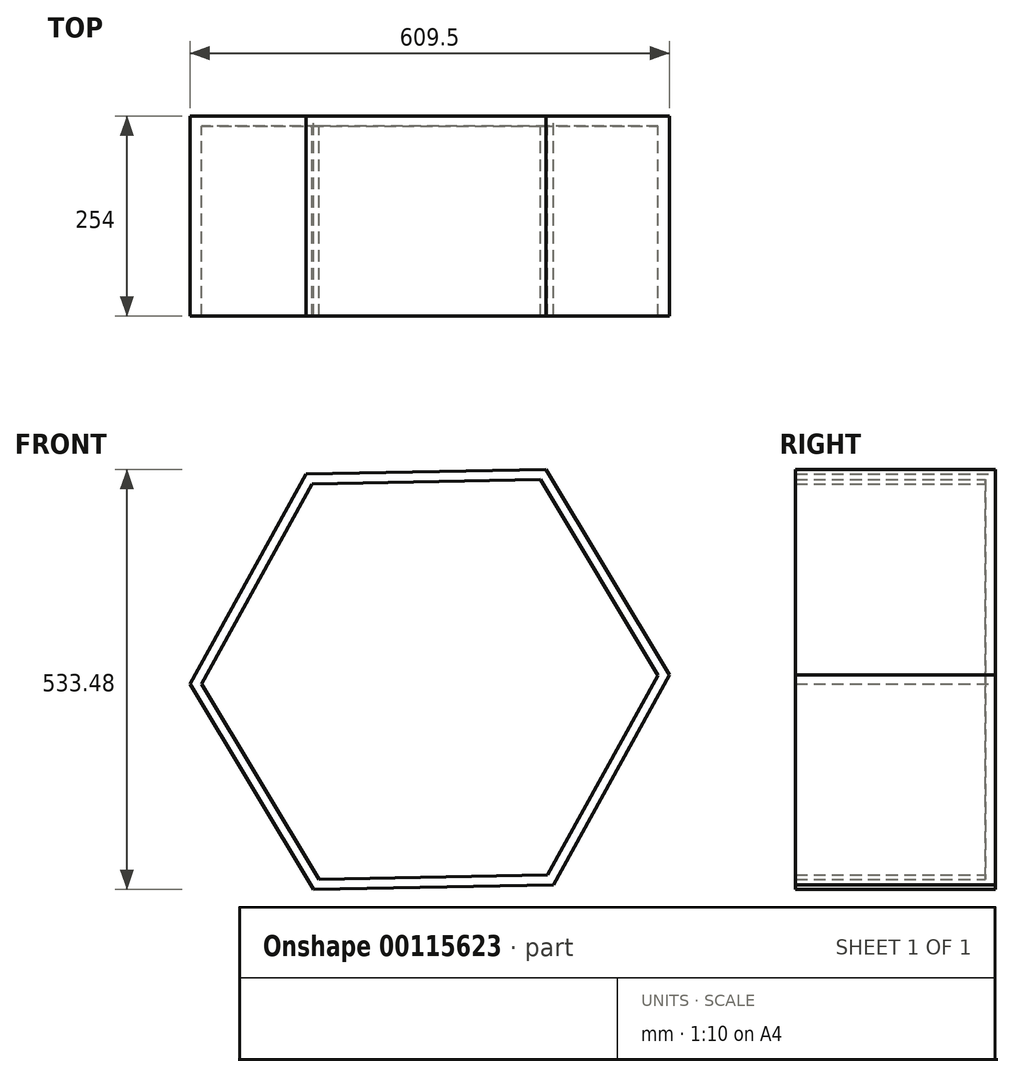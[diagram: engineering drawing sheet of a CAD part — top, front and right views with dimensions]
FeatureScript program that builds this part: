
annotation { "Feature Type Name" : "Feature", "Feature Type Description" : "" }
export const myFeature = defineFeature(function(context is Context, id is Id, definition is map)
    precondition{}
    {
        {
            var Q0;
            Q0=qCreatedBy(makeId("Front.planeOp"),FACE);
            var sketch = newSketch(context, id + "F0", { "sketchPlane" : qUnion([Q0])});
            skCircle(sketch, "E0.cCircle", {"center": v(0, 0) * mm, "radius": 263.96 * mm, "construction": true});
            skLineSegment(sketch, "E0.0", {"start": v(-304.75, -5.64) * mm, "end": v(-157.26, 261.1) * mm});
            skLineSegment(sketch, "E0.1", {"start": v(-157.26, 261.1) * mm, "end": v(147.5, 266.74) * mm});
            skLineSegment(sketch, "E0.2", {"start": v(147.5, 266.74) * mm, "end": v(304.75, 5.64) * mm});
            skLineSegment(sketch, "E0.3", {"start": v(304.75, 5.64) * mm, "end": v(157.26, -261.1) * mm});
            skLineSegment(sketch, "E0.4", {"start": v(157.26, -261.1) * mm, "end": v(-147.5, -266.74) * mm});
            skLineSegment(sketch, "E0.5", {"start": v(-147.5, -266.74) * mm, "end": v(-304.75, -5.64) * mm});
            skPoint(sketch, "E0.0.midPoint", {"position": v(-231, 127.73) * mm});
            skSolve(sketch);
        }
        {
            var Q0;
            Q0=makeQuery(id+"F0.imprint","IMPRINT",FACE,{"disambiguationData":[TD([[makeQuery(id+"F0.imprint","IMPRINT",EDGE,{"derivedFrom":sQuery(id+"F0.wireOp",EDGE,"E0.0")}),-1.0]])]});
            extrude(context, id + "F1", {"entities" : qUnion([Q0]), "depth" : 254 * mm});
        }
        {
            var Q0;
            Q0=makeQuery(id+"F1.opExtrude","CAP_FACE",FACE,{"disambiguationData":[OSD([sQuery(id+"F0.wireOp",EDGE,"E0.0"),sQuery(id+"F0.wireOp",EDGE,"E0.1"),sQuery(id+"F0.wireOp",EDGE,"E0.2"),sQuery(id+"F0.wireOp",EDGE,"E0.3"),sQuery(id+"F0.wireOp",EDGE,"E0.4"),sQuery(id+"F0.wireOp",EDGE,"E0.5")])],"isStart":false});
            shell(context, id + "F2", {"entities" : qUnion([Q0]), "thickness" : 12.7 * mm});
        }
        {
            var Q0;
            Q0=makeQuery(id+"F1.opExtrude","SWEPT_BODY",BODY,{"disambiguationData":[OSD([sQuery(id+"F0.wireOp",EDGE,"E0.0"),sQuery(id+"F0.wireOp",EDGE,"E0.1"),sQuery(id+"F0.wireOp",EDGE,"E0.2"),sQuery(id+"F0.wireOp",EDGE,"E0.3"),sQuery(id+"F0.wireOp",EDGE,"E0.4"),sQuery(id+"F0.wireOp",EDGE,"E0.5")])]});
            transform(context, id + "F3", {"entities" : qUnion([Q0]), "transformType" : TransformType.TRANSLATION_3D, "dx" : 557.77 * mm, "dy" : 0 * mm, "dz" : 309.68 * mm, "makeCopy" : true});
        }
        {
            var Q0;
            Q0=makeQuery(id+"F3.opPattern","COPY",BODY,{"derivedFrom":makeQuery(id+"F1.opExtrude","SWEPT_BODY",BODY,{"disambiguationData":[OSD([sQuery(id+"F0.wireOp",EDGE,"E0.0"),sQuery(id+"F0.wireOp",EDGE,"E0.1"),sQuery(id+"F0.wireOp",EDGE,"E0.2"),sQuery(id+"F0.wireOp",EDGE,"E0.3"),sQuery(id+"F0.wireOp",EDGE,"E0.4"),sQuery(id+"F0.wireOp",EDGE,"E0.5")])]}),"instanceName":"1"});
            deleteBodies(context, id + "F4", {"entities" : qUnion([Q0])});
        }
    });
